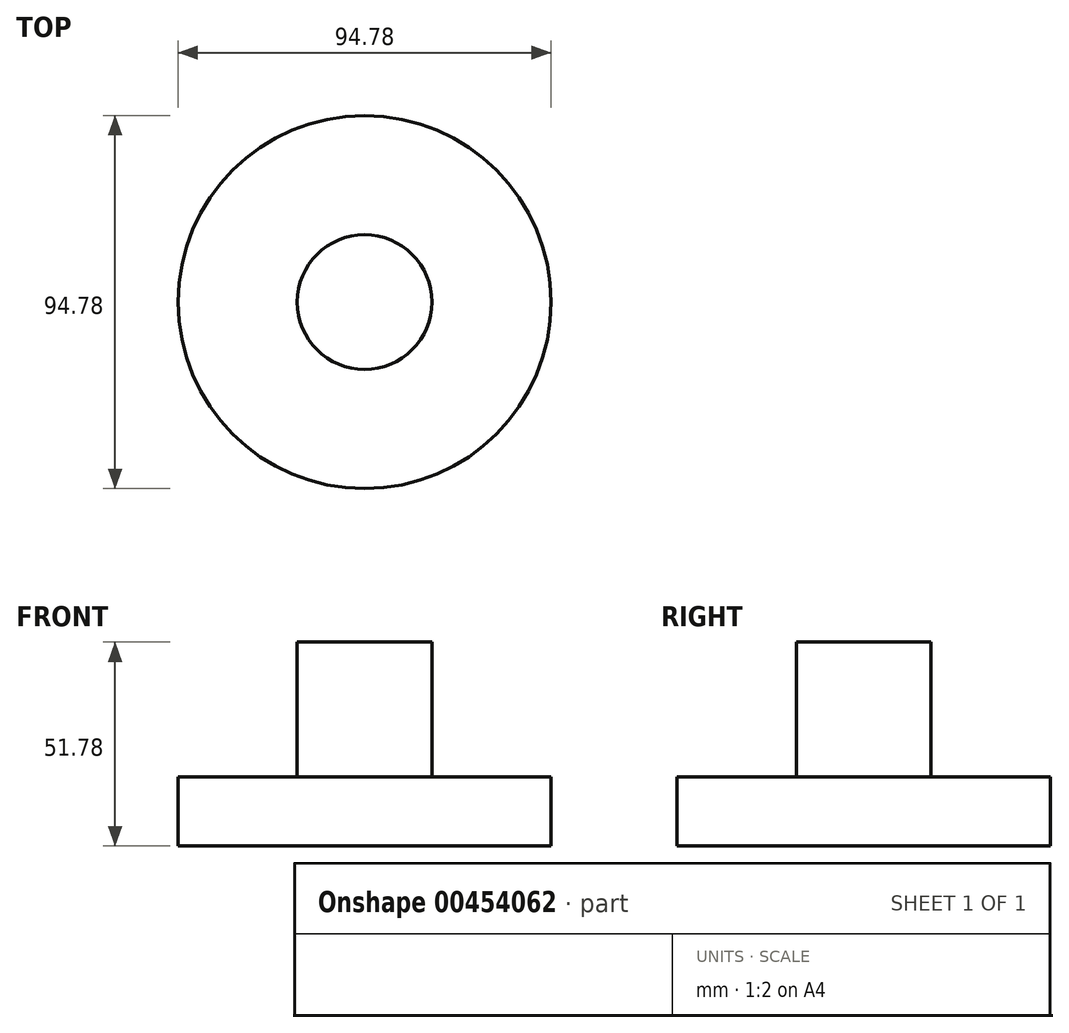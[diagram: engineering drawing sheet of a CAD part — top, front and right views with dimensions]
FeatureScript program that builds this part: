
annotation { "Feature Type Name" : "Feature", "Feature Type Description" : "" }
export const myFeature = defineFeature(function(context is Context, id is Id, definition is map)
    precondition{}
    {
        {
            var Q0;
            Q0=qCreatedBy(makeId("Front.planeOp"),FACE);
            var sketch = newSketch(context, id + "F0", { "sketchPlane" : qUnion([Q0])});
            skLineSegment(sketch, "E0.bottom", {"start": v(-47.4, 51.78) * mm, "end": v(0, 51.78) * mm});
            skLineSegment(sketch, "E0.top", {"start": v(-47.4, 0) * mm, "end": v(0, 0) * mm});
            skLineSegment(sketch, "E0.left", {"start": v(-47.4, 51.78) * mm, "end": v(-47.4, 0) * mm});
            skLineSegment(sketch, "E0.right", {"start": v(0, 51.78) * mm, "end": v(0, 0) * mm});
            skSolve(sketch);
        }
        {
            var Q0;
            Q0 = qSketchRegion(id + "F0", true);
            var Q1;
            Q1=sQuery(id+"F0.wireOp",EDGE,"E0.right");
            revolve(context, id + "F1", {"entities" : qUnion([Q0]), "axis" : qUnion([Q1]), "revolveType" : RevolveType.FULL});
        }
        {
            var Q0;
            Q0=qCreatedBy(makeId("Front.planeOp"),FACE);
            var sketch = newSketch(context, id + "F2", { "sketchPlane" : qUnion([Q0])});
            skLineSegment(sketch, "E1.bottom", {"start": v(-51.78, 54.41) * mm, "end": v(-17.11, 54.41) * mm});
            skLineSegment(sketch, "E1.top", {"start": v(-51.78, 17.55) * mm, "end": v(-17.11, 17.55) * mm});
            skLineSegment(sketch, "E1.left", {"start": v(-51.78, 54.41) * mm, "end": v(-51.78, 17.55) * mm});
            skLineSegment(sketch, "E1.right", {"start": v(-17.11, 54.41) * mm, "end": v(-17.11, 17.55) * mm});
            skLineSegment(sketch, "E2", {"start": v(0, 68.9) * mm, "end": v(0, 0) * mm});
            skSolve(sketch);
        }
        {
            var Q0;
            Q0 = qSketchRegion(id + "F2", true);
            var Q1;
            Q1=sQuery(id+"F2.wireOp",EDGE,"E2");
            revolve(context, id + "F3", {"operationType" : NewBodyOperationType.REMOVE, "entities" : qUnion([Q0]), "axis" : qUnion([Q1]), "revolveType" : RevolveType.FULL, "oppositeDirection" : true});
        }
    });
